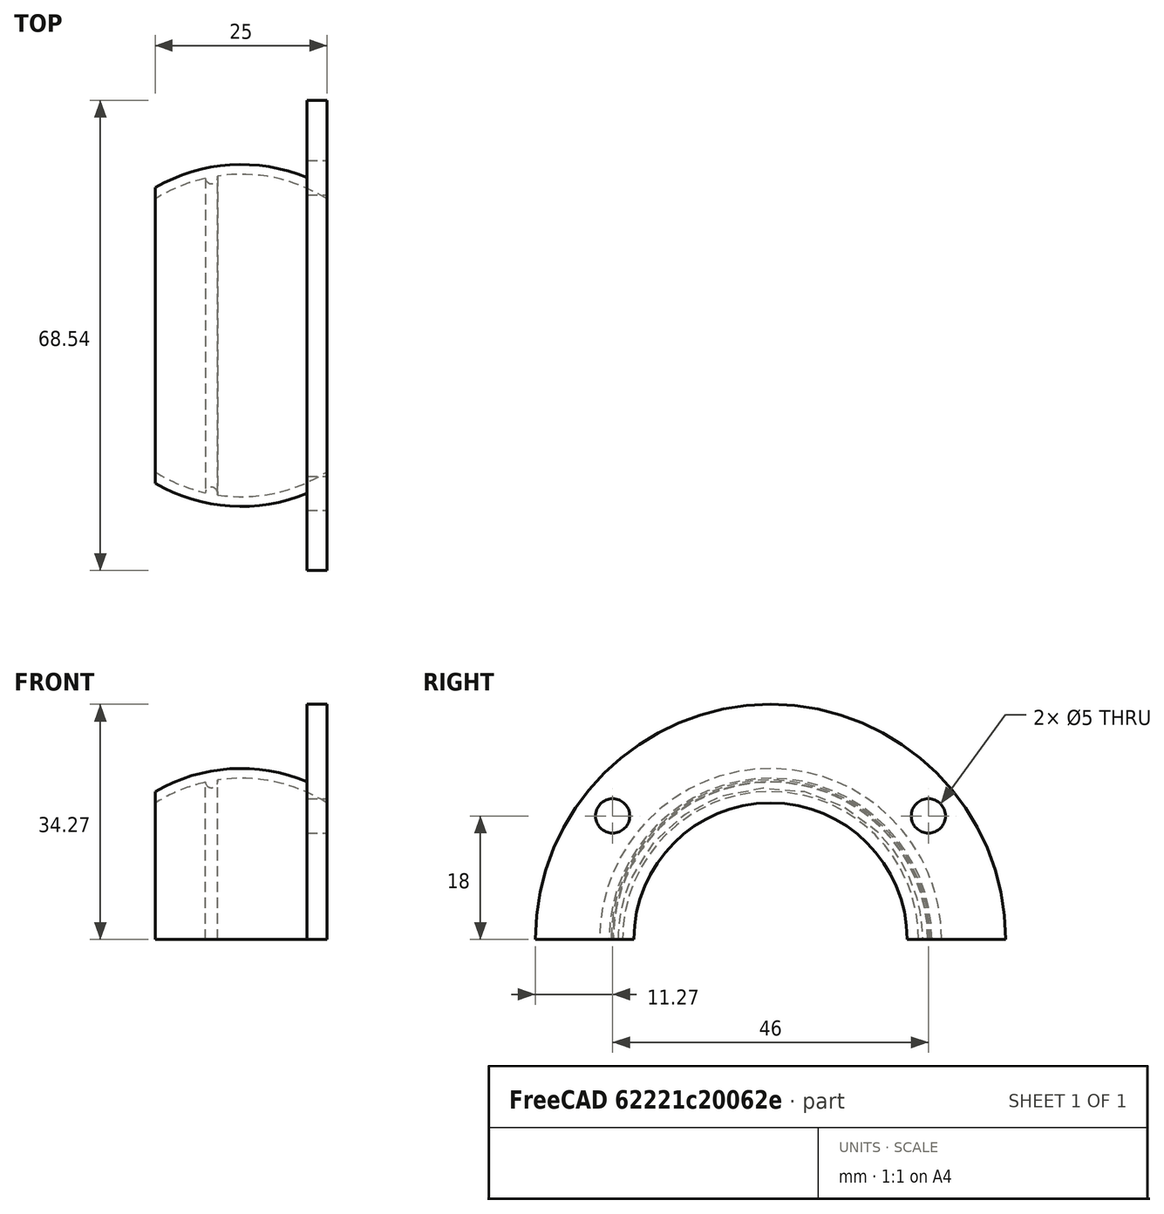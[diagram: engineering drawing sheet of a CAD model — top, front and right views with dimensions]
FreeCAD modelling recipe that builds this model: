
FCSTD DOCUMENT  (FreeCAD 0.18R16110 (Git))
Label: newbearinghub
License: All rights reserved
LicenseURL: http://en.wikipedia.org/wiki/All_rights_reserved
objects: Mesh::Feature×3, Part::Cylinder×2, Part::Cut×2, Sketcher::SketchObject×1, Part::Revolution×1
note: 6 computed .brp shape members not serialized (recipe doc carries the construction recipe); baked Part::Feature solids carry a one-line shape summary decoded from their .brp

FEATURE [Sketcher::SketchObject] Sketch
  sketch-geometry (12):
    g0: ArcOfCircle CenterX=0 CenterY=0 CenterZ=0 NormalX=0 NormalY=0 NormalZ=1 AngleXU=0 Radius=23.5 StartAngle=1.00994 EndAngle=1.71812
    g1: ArcOfCircle CenterX=0 CenterY=0 CenterZ=0 NormalX=0 NormalY=0 NormalZ=1 AngleXU=0 Radius=24.9221 StartAngle=1.17549 EndAngle=2.0962
    g2: LineSegment StartX=12.5 StartY=23 StartZ=0 EndX=12.5 EndY=19.8997 EndZ=0
    g3: LineSegment StartX=-12.5 StartY=21.5606 StartZ=0 EndX=-12.5 EndY=19.8997 EndZ=0
    g4: LineSegment [constr] StartX=-12.5 StartY=19.8997 StartZ=0 EndX=12.5 EndY=19.8997 EndZ=0
    g5: GeomPoint X=-7.36008 Y=22.3177 Z=0
    g6: GeomPoint X=-7.3108 Y=22.8515 Z=0
    g7: ArcOfCircle CenterX=-4.32144 CenterY=23.0217 CenterZ=0 NormalX=0 NormalY=0 NormalZ=1 AngleXU=0 Radius=0.9 StartAngle=3.26154 EndAngle=6.53441
    g8: ArcOfCircle CenterX=-0.000204642 CenterY=9.13448e-05 CenterZ=0 NormalX=0 NormalY=0 NormalZ=1 AngleXU=0 Radius=23.4998 StartAngle=1.79457 EndAngle=2.13165
    g9: LineSegment StartX=9.59736 StartY=23 StartZ=0 EndX=9.59736 EndY=34.2713 EndZ=0
    g10: LineSegment StartX=9.59736 StartY=34.2713 StartZ=0 EndX=12.5 EndY=34.2713 EndZ=0
    g11: LineSegment StartX=12.5 StartY=34.2713 StartZ=0 EndX=12.5 EndY=23 EndZ=0
  constraints (24):
    c: Coincident(g0,g-1)
    c: Coincident(g1,g0)
    c: Coincident(g2,g0)
    c: Vertical(g2)
    c: Coincident(g3,g1)
    c: Coincident(g3,g8)
    c: Vertical(g3)
    c: Symmetric(g0,g8,g-2)
    c: Coincident(g4,g8)
    c: Coincident(g4,g0)
    c: Radius(g0) = 23.5
    c: DistanceX(g4,g4) = 25
    c: PointOnObject(g5,g0)
    c: Radius(g7) = 0.9
    c: Coincident(g7,g0)
    c: Coincident(g8,g7)
    c: DistanceY(g11) = 23
    c: Coincident(g1,g9)
    c: Coincident(g9,g10)
    c: Horizontal(g10)
    c: Coincident(g10,g11)
    c: Vertical(g11)
    c: Vertical(g9)
    c: Coincident(g2,g11)
FEATURE [Part::Revolution] Revolve
  Angle = 180
  Axis = (1,0,0)
  Base = (0,0,0)
  FaceMakerClass = Part::FaceMakerBullseye
  Solid = true
  Source = -> Sketch
  Symmetric = false
FEATURE [Mesh::Feature] handle3_5  label="handle3.5"
  Placement = pos=(5.5,30.5,0) rot=(0,0,1;0rad)
FEATURE [Mesh::Feature] handle3_006  label="handle3.006"
  Placement = pos=(5.5,-30.5,0) rot=(0,0,1;0rad)
FEATURE [Mesh::Feature] handle3_5nohole  label="handle3.5nohole"
  Placement = pos=(5.5,-1.75,30.5) rot=(1,0,0;4.71239rad)
FEATURE [Part::Cylinder] Cylinder
  Angle = 360
  AttacherType = Attacher::AttachEngine3D
  Height = 10
  Placement = pos=(5,23,18) rot=(0,-1,0;4.71239rad)
  Radius = 2.5
FEATURE [Part::Cylinder] Cylinder001
  Angle = 360
  AttacherType = Attacher::AttachEngine3D
  Height = 10
  Placement = pos=(5,-23,18) rot=(0,1,0;1.5708rad)
  Radius = 2.5
FEATURE [Part::Cut] Cut
  Base = -> Revolve
  Tool = -> Cylinder
FEATURE [Part::Cut] Cut001
  Base = -> Cut
  Tool = -> Cylinder001
